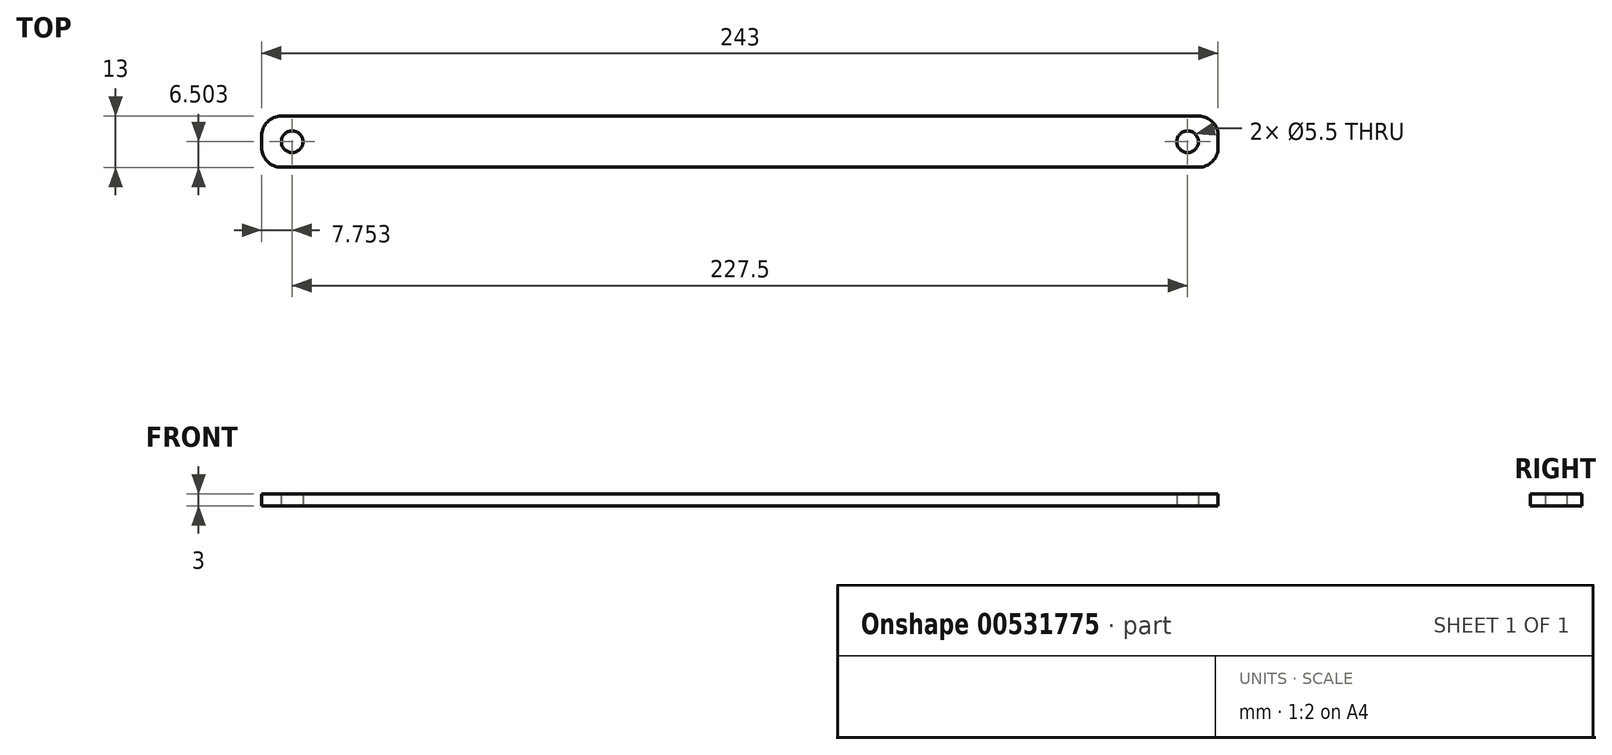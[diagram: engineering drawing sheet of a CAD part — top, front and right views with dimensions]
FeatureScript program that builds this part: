
annotation { "Feature Type Name" : "Feature", "Feature Type Description" : "" }
export const myFeature = defineFeature(function(context is Context, id is Id, definition is map)
    precondition{}
    {
        {
            var Q0;
            Q0=qCreatedBy(makeId("Top.planeOp"),FACE);
            var sketch = newSketch(context, id + "F0", { "sketchPlane" : qUnion([Q0])});
            skLineSegment(sketch, "E0.bottom", {"start": v(-111.3, 1.2) * mm, "end": v(121.7, 1.2) * mm});
            skLineSegment(sketch, "E0.top", {"start": v(-111.3, -11.8) * mm, "end": v(121.7, -11.8) * mm});
            skLineSegment(sketch, "E0.left", {"start": v(-116.3, -3.8) * mm, "end": v(-116.3, -6.8) * mm});
            skLineSegment(sketch, "E0.right", {"start": v(126.7, -3.8) * mm, "end": v(126.7, -6.8) * mm});
            skPoint(sketch, "E1.visualSharp", {"position": v(126.7, 1.2) * mm});
            skArc(sketch, "E1.filletArc", {"start": v(126.7, -3.8) * mm, "mid": v(125.24, -0.27) * mm, "end": v(121.7, 1.2) * mm});
            skPoint(sketch, "E2.visualSharp", {"position": v(126.7, -11.8) * mm});
            skArc(sketch, "E2.filletArc", {"start": v(121.7, -11.8) * mm, "mid": v(125.24, -10.34) * mm, "end": v(126.7, -6.8) * mm});
            skPoint(sketch, "E3.visualSharp", {"position": v(-116.3, 1.2) * mm});
            skArc(sketch, "E3.filletArc", {"start": v(-111.3, 1.2) * mm, "mid": v(-114.83, -0.27) * mm, "end": v(-116.3, -3.8) * mm});
            skPoint(sketch, "E4.visualSharp", {"position": v(-116.3, -11.8) * mm});
            skArc(sketch, "E4.filletArc", {"start": v(-116.3, -6.8) * mm, "mid": v(-114.83, -10.34) * mm, "end": v(-111.3, -11.8) * mm});
            skCircle(sketch, "E5", {"center": v(118.95, -5.3) * mm, "radius": 2.75 * mm});
            skCircle(sketch, "E6", {"center": v(-108.55, -5.3) * mm, "radius": 2.75 * mm});
            skSolve(sketch);
        }
        {
            var Q0;
            Q0=makeQuery(id+"F0.imprint","IMPRINT",FACE,{"disambiguationData":[TD([[makeQuery(id+"F0.imprint","IMPRINT",EDGE,{"derivedFrom":sQuery(id+"F0.wireOp",EDGE,"E0.bottom")}),-1.0]])]});
            extrude(context, id + "F1", {"entities" : qUnion([Q0]), "depth" : 3 * mm, "offsetDistance" : 25 * mm});
        }
    });
